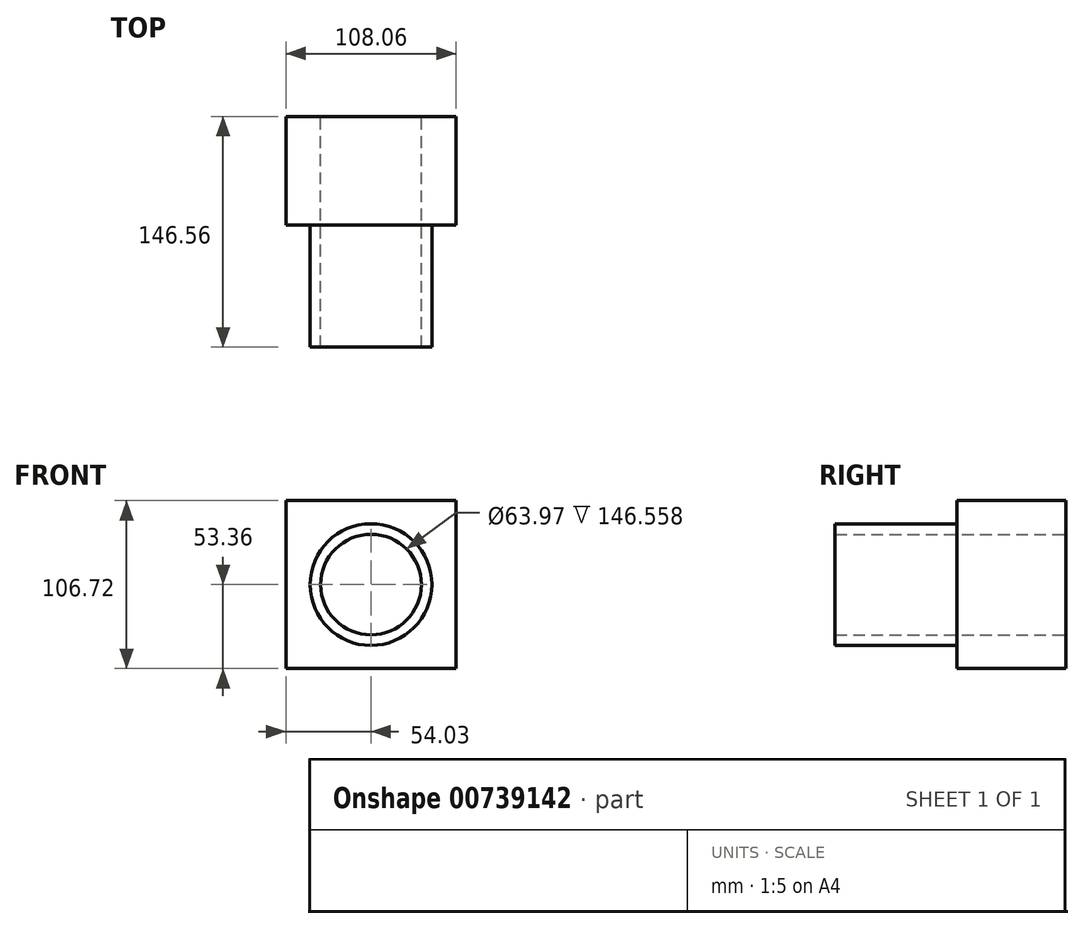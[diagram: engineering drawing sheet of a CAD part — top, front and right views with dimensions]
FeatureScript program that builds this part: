
annotation { "Feature Type Name" : "Feature", "Feature Type Description" : "" }
export const myFeature = defineFeature(function(context is Context, id is Id, definition is map)
    precondition{}
    {
        {
            var Q0;
            Q0=qCreatedBy(makeId("Front.planeOp"),FACE);
            var sketch = newSketch(context, id + "F0", { "sketchPlane" : qUnion([Q0])});
            skCircle(sketch, "E0", {"center": v(0, 0) * mm, "radius": 38.66 * mm});
            skLineSegment(sketch, "E1.bottom", {"start": v(54.03, 53.36) * mm, "end": v(-54.03, 53.36) * mm});
            skLineSegment(sketch, "E1.top", {"start": v(54.03, -53.36) * mm, "end": v(-54.03, -53.36) * mm});
            skLineSegment(sketch, "E1.left", {"start": v(54.03, 53.36) * mm, "end": v(54.03, -53.36) * mm});
            skLineSegment(sketch, "E1.right", {"start": v(-54.03, 53.36) * mm, "end": v(-54.03, -53.36) * mm});
            skCircle(sketch, "E2", {"center": v(0, 0) * mm, "radius": 31.98 * mm});
            skSolve(sketch);
        }
        {
            var Q0;
            Q0 = qSketchRegion(id + "F0", true);
            extrude(context, id + "F1", {"entities" : qUnion([Q0]), "depth" : 69.1 * mm, "offsetDistance" : 25.4 * mm});
        }
        {
            var Q0;
            Q0=makeQuery(id+"F0.imprint","IMPRINT",FACE,{"disambiguationData":[TD([[makeQuery(id+"F0.imprint","IMPRINT",EDGE,{"derivedFrom":sQuery(id+"F0.wireOp",EDGE,"E0")}),1.0]])]});
            extrude(context, id + "F2", {"entities" : qUnion([Q0]), "operationType" : NewBodyOperationType.ADD, "depth" : 146.56 * mm, "offsetDistance" : 25.4 * mm});
        }
    });
